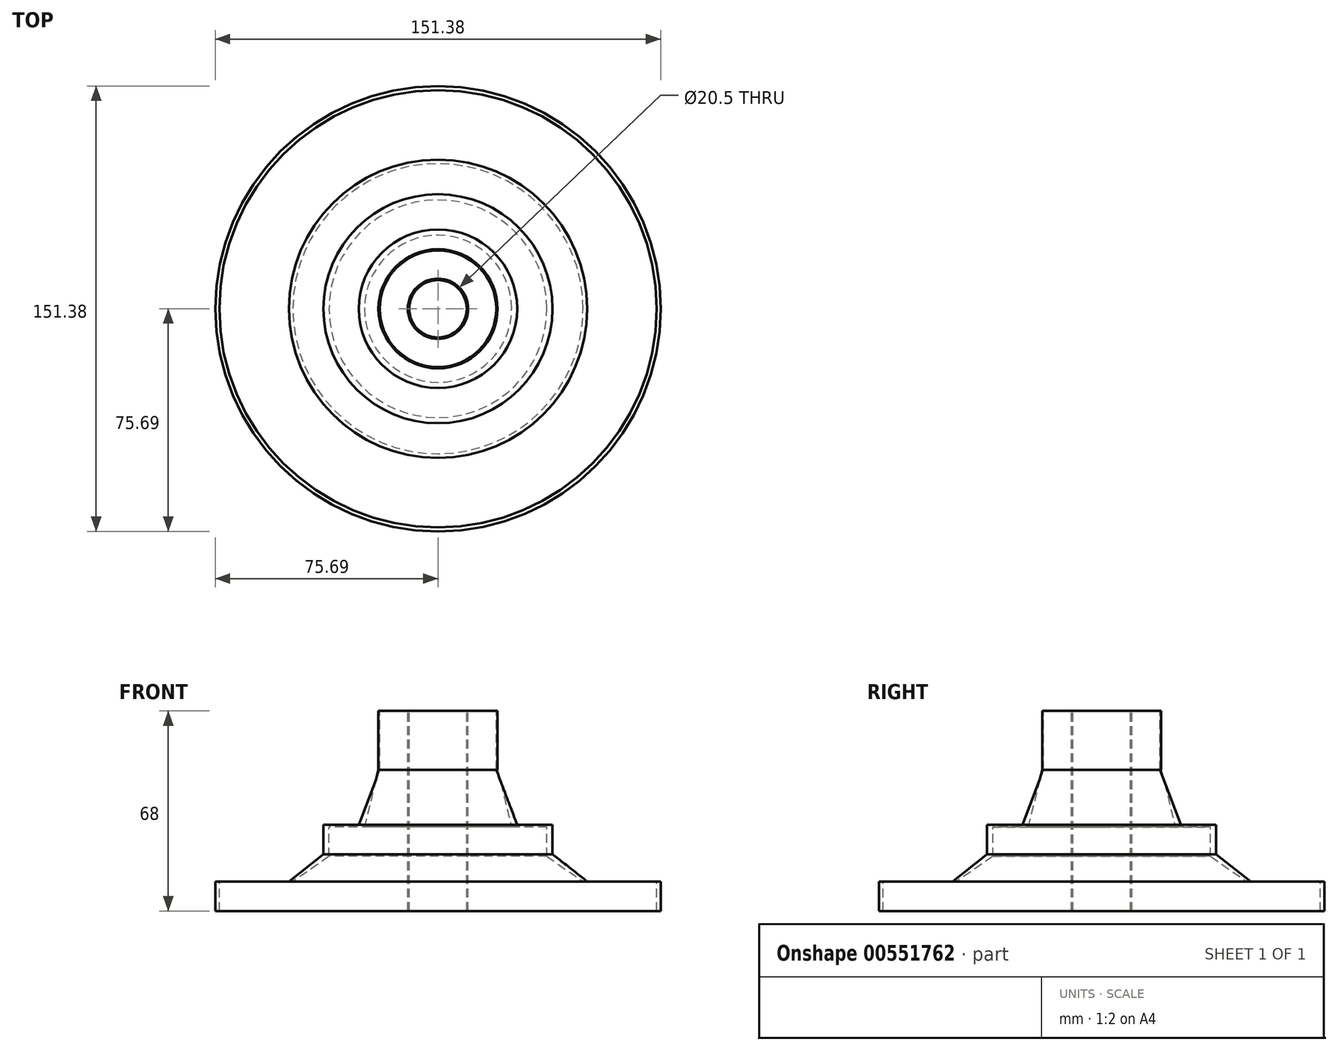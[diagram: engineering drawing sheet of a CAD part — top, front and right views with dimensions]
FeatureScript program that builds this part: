
annotation { "Feature Type Name" : "Feature", "Feature Type Description" : "" }
export const myFeature = defineFeature(function(context is Context, id is Id, definition is map)
    precondition{}
    {
        {
            var Q0;
            Q0=qCreatedBy(makeId("Front.planeOp"),FACE);
            var sketch = newSketch(context, id + "F0", { "sketchPlane" : qUnion([Q0])});
            skLineSegment(sketch, "E0", {"start": v(0, 68) * mm, "end": v(10, 68) * mm, "construction": true});
            skLineSegment(sketch, "E1", {"start": v(10, 68) * mm, "end": v(-10, 68) * mm, "construction": true});
            skLineSegment(sketch, "E2", {"start": v(-10, 68) * mm, "end": v(-10, 0) * mm, "construction": true});
            skLineSegment(sketch, "E3", {"start": v(-10, 0) * mm, "end": v(10, 0) * mm, "construction": true});
            skLineSegment(sketch, "E4", {"start": v(10, 0) * mm, "end": v(10, 68) * mm, "construction": true});
            skLineSegment(sketch, "E5", {"start": v(10, 68) * mm, "end": v(20, 68) * mm, "construction": true});
            skLineSegment(sketch, "E6", {"start": v(20, 68) * mm, "end": v(-20, 68) * mm, "construction": true});
            skLineSegment(sketch, "E7", {"start": v(-20, 68) * mm, "end": v(-20, 48) * mm, "construction": true});
            skLineSegment(sketch, "E8", {"start": v(20, 68) * mm, "end": v(20, 48) * mm, "construction": true});
            skLineSegment(sketch, "E9", {"start": v(0, 68) * mm, "end": v(0, 27.84) * mm, "construction": true});
            skLineSegment(sketch, "E10", {"start": v(0, 27.84) * mm, "end": v(-37.5, 27.84) * mm, "construction": true});
            skLineSegment(sketch, "E11", {"start": v(0, 27.84) * mm, "end": v(37.5, 27.84) * mm, "construction": true});
            skLineSegment(sketch, "E12", {"start": v(0, 68) * mm, "end": v(0, 18) * mm, "construction": true});
            skLineSegment(sketch, "E13", {"start": v(0, 68) * mm, "end": v(0, 10) * mm, "construction": true});
            skPoint(sketch, "E13.endSnap0", {"position": v(0, 43) * mm});
            skLineSegment(sketch, "E14", {"start": v(0, 10) * mm, "end": v(50, 10) * mm, "construction": true});
            skLineSegment(sketch, "E15", {"start": v(50, 10) * mm, "end": v(-50, 10) * mm, "construction": true});
            skLineSegment(sketch, "E16", {"start": v(0, 27.84) * mm, "end": v(-25, 27.84) * mm, "construction": true});
            skLineSegment(sketch, "E17", {"start": v(0, 27.84) * mm, "end": v(25, 27.84) * mm, "construction": true});
            skSolve(sketch);
        }
        {
            var Q0;
            Q0=qCreatedBy(makeId("Front.planeOp"),FACE);
            var sketch = newSketch(context, id + "F1", { "sketchPlane" : qUnion([Q0])});
            skLineSegment(sketch, "E18", {"start": v(-74.31, 0) * mm, "end": v(75.69, 0) * mm});
            skLineSegment(sketch, "E19", {"start": v(75.69, 0) * mm, "end": v(75.69, 10) * mm});
            skLineSegment(sketch, "E20", {"start": v(75.69, 10) * mm, "end": v(50.69, 10) * mm});
            skLineSegment(sketch, "E21", {"start": v(-74.31, 0) * mm, "end": v(-74.31, 10) * mm});
            skLineSegment(sketch, "E22", {"start": v(-74.31, 10) * mm, "end": v(-49.31, 10) * mm});
            skLineSegment(sketch, "E23", {"start": v(-10.25, 68) * mm, "end": v(-20.25, 68) * mm});
            skLineSegment(sketch, "E24", {"start": v(-20.25, 68) * mm, "end": v(-20.25, 48) * mm});
            skLineSegment(sketch, "E25", {"start": v(9.8, 68) * mm, "end": v(19.8, 68) * mm});
            skLineSegment(sketch, "E26", {"start": v(19.8, 68) * mm, "end": v(19.8, 48) * mm});
            skLineSegment(sketch, "E27", {"start": v(-10.25, 68) * mm, "end": v(-10.25, 0) * mm});
            skLineSegment(sketch, "E28", {"start": v(-10.25, 0) * mm, "end": v(9.75, 0) * mm});
            skLineSegment(sketch, "E29", {"start": v(9.75, 0) * mm, "end": v(9.8, 68) * mm});
            skLineSegment(sketch, "E30", {"start": v(38.93, 29.31) * mm, "end": v(38.93, 19.31) * mm});
            skLineSegment(sketch, "E31", {"start": v(38.93, 19.31) * mm, "end": v(50.69, 10) * mm});
            skLineSegment(sketch, "E32", {"start": v(-37, 28.57) * mm, "end": v(-37, 18.57) * mm});
            skLineSegment(sketch, "E33", {"start": v(-37, 18.57) * mm, "end": v(-49.31, 10) * mm});
            skLineSegment(sketch, "E34", {"start": v(-37, 28.57) * mm, "end": v(-25, 28.57) * mm});
            skLineSegment(sketch, "E35", {"start": v(38.93, 29.31) * mm, "end": v(26.93, 29.31) * mm});
            skLineSegment(sketch, "E36", {"start": v(-25, 28.57) * mm, "end": v(-20.25, 48) * mm});
            skLineSegment(sketch, "E37", {"start": v(19.8, 48) * mm, "end": v(26.93, 29.31) * mm});
            skSolve(sketch);
        }
        {
            var Q0;
            Q0=qSketchRegion(id+"F1",true);
            var Q1;
            Q1=sQuery(id+"F0.wireOp",EDGE,"E13");
            revolve(context, id + "F2", {"entities" : qUnion([Q0]), "axis" : qUnion([Q1]), "revolveType" : RevolveType.FULL});
        }
    });
